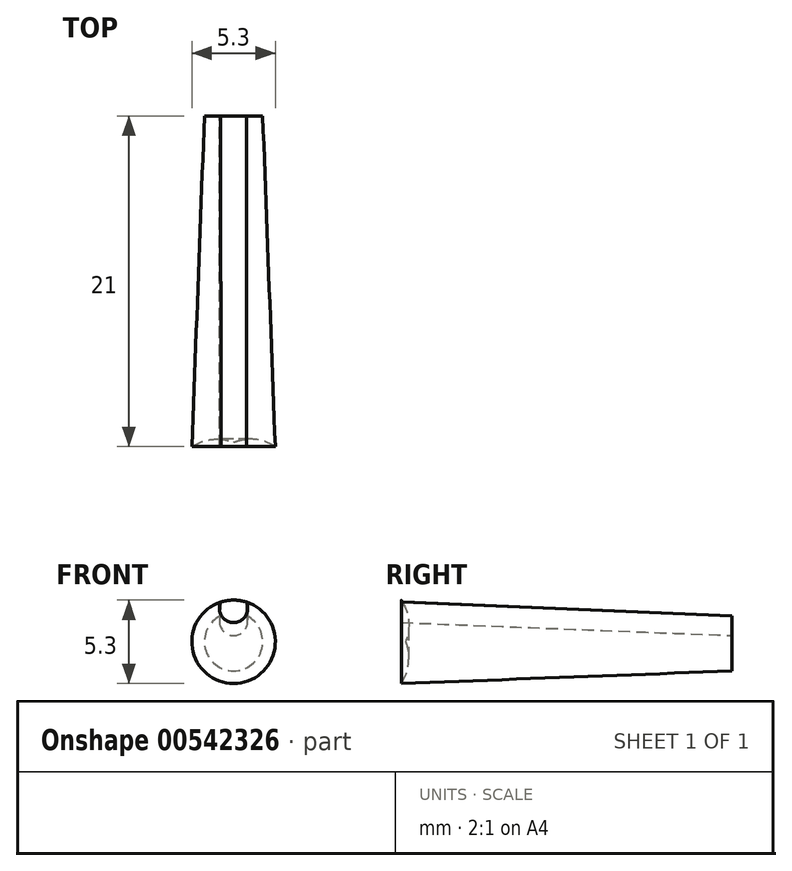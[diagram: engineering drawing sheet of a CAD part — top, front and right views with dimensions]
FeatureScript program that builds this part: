
annotation { "Feature Type Name" : "Feature", "Feature Type Description" : "" }
export const myFeature = defineFeature(function(context is Context, id is Id, definition is map)
    precondition{}
    {
        {
            var Q0;
            Q0=qCreatedBy(makeId("Front.planeOp"),FACE);
            var sketch = newSketch(context, id + "F0", { "sketchPlane" : qUnion([Q0])});
            skArc(sketch, "E0", {"start": v(-0.83, 1.65) * mm, "mid": v(0, -1.85) * mm, "end": v(0.83, 1.65) * mm});
            skArc(sketch, "E1", {"start": v(-0.83, 1.65) * mm, "mid": v(0, 0.4) * mm, "end": v(0.83, 1.65) * mm});
            skSolve(sketch);
        }
        {
            var Q0;
            Q0=makeQuery(id+"F0.imprint","IMPRINT",FACE,{"disambiguationData":[TD([[makeQuery(id+"F0.imprint","IMPRINT",EDGE,{"derivedFrom":sQuery(id+"F0.wireOp",EDGE,"E0")}),1.0]])]});
            cPlane(context, id + "F1", {"entities" : qUnion([Q0]), "cplaneType" : CPlaneType.OFFSET, "offset" : 21 * mm, "width" : 150 * mm, "height" : 150 * mm});
        }
        {
            var Q0;
            Q0=qCreatedBy(id+"F1.planeOp",FACE);
            var sketch = newSketch(context, id + "F2", { "sketchPlane" : qUnion([Q0])});
            skArc(sketch, "E2", {"start": v(-0.8, 2.52) * mm, "mid": v(0, -2.65) * mm, "end": v(0.8, 2.52) * mm});
            skArc(sketch, "E3", {"start": v(-0.8, 2.52) * mm, "mid": v(0, 1.23) * mm, "end": v(0.8, 2.52) * mm});
            skSolve(sketch);
        }
        {
            var Q0;
            Q0=makeQuery(id+"F0.imprint","IMPRINT",FACE,{"disambiguationData":[TD([[makeQuery(id+"F0.imprint","IMPRINT",EDGE,{"derivedFrom":sQuery(id+"F0.wireOp",EDGE,"E0")}),1.0]])]});
            var Q1;
            Q1=makeQuery(id+"F2.imprint","IMPRINT",FACE,{"disambiguationData":[TD([[makeQuery(id+"F2.imprint","IMPRINT",EDGE,{"derivedFrom":sQuery(id+"F2.wireOp",EDGE,"E2")}),1.0]])]});
            loft(context, id + "F3", {"sheetProfilesArray" : [{ "sheetProfileEntities" : qUnion([Q0]) }, { "sheetProfileEntities" : qUnion([Q1]) }]});
        }
        {
            var Q0;
            Q0=qCreatedBy(makeId("Top.planeOp"),FACE);
            var sketch = newSketch(context, id + "F4", { "sketchPlane" : qUnion([Q0])});
            skPoint(sketch, "E4.end.orphan", {"position": v(0, -28.3) * mm});
            skArc(sketch, "E5", {"start": v(-2.65, -21) * mm, "mid": v(-3.62, -24.74) * mm, "end": v(0, -26.1) * mm});
            skLineSegment(sketch, "E6", {"start": v(-2.65, -21) * mm, "end": v(0, -21) * mm});
            skLineSegment(sketch, "E7", {"start": v(0, -21) * mm, "end": v(0, -26.1) * mm});
            skSolve(sketch);
        }
        {
            var Q0;
            Q0 = qSketchRegion(id + "F4", true);
            var Q1;
            Q1=sQuery(id+"F4.wireOp",EDGE,"E7");
            revolve(context, id + "F5", {"operationType" : NewBodyOperationType.ADD, "entities" : qUnion([Q0]), "axis" : qUnion([Q1]), "revolveType" : RevolveType.FULL});
        }
    });
